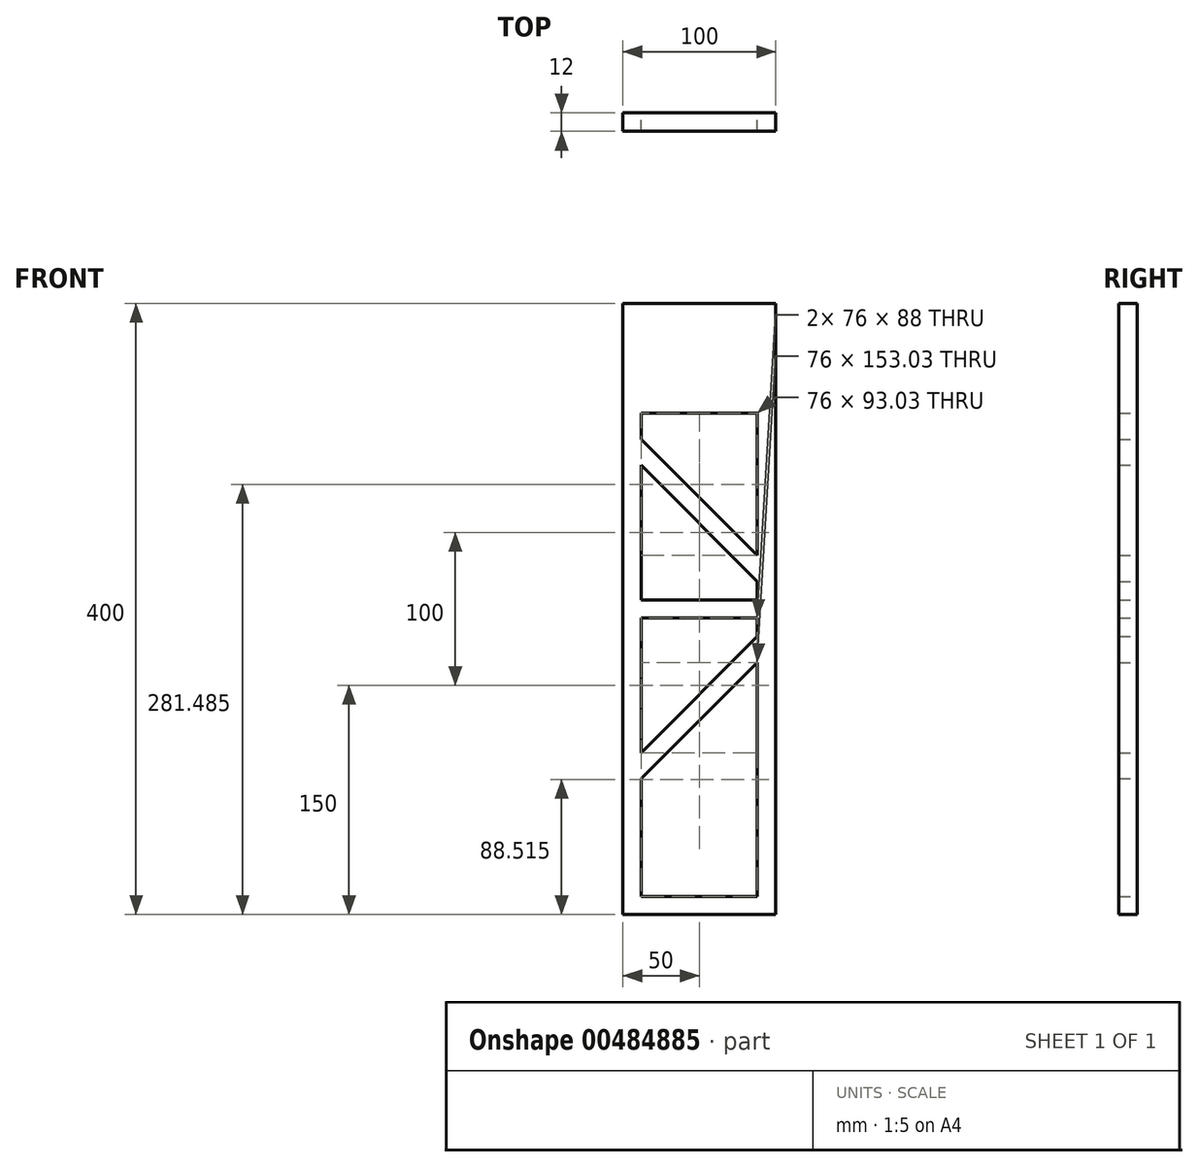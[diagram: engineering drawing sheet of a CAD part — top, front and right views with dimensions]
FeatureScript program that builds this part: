
annotation { "Feature Type Name" : "Feature", "Feature Type Description" : "" }
export const myFeature = defineFeature(function(context is Context, id is Id, definition is map)
    precondition{}
    {
        {
            var Q0;
            Q0=qCreatedBy(makeId("Front.planeOp"),FACE);
            var sketch = newSketch(context, id + "F0", { "sketchPlane" : qUnion([Q0])});
            skLineSegment(sketch, "E0", {"start": v(0, 0) * mm, "end": v(50, 0) * mm});
            skLineSegment(sketch, "E1", {"start": v(50, 0) * mm, "end": v(50, 400) * mm});
            skLineSegment(sketch, "E2", {"start": v(0, 0) * mm, "end": v(-50, 0) * mm});
            skLineSegment(sketch, "E3", {"start": v(-50, 0) * mm, "end": v(-50, 400) * mm});
            skLineSegment(sketch, "E4", {"start": v(-50, 400) * mm, "end": v(50, 400) * mm});
            skLineSegment(sketch, "E5", {"start": v(-50, 388) * mm, "end": v(-38, 388) * mm, "construction": true});
            skLineSegment(sketch, "E6", {"start": v(-38, 388) * mm, "end": v(-38, 400) * mm, "construction": true});
            skLineSegment(sketch, "E7", {"start": v(38, 400) * mm, "end": v(38, 388) * mm, "construction": true});
            skLineSegment(sketch, "E8", {"start": v(38, 388) * mm, "end": v(50, 388) * mm, "construction": true});
            skLineSegment(sketch, "E9", {"start": v(38, 0) * mm, "end": v(38, 12) * mm, "construction": true});
            skLineSegment(sketch, "E10", {"start": v(38, 12) * mm, "end": v(50, 12) * mm, "construction": true});
            skLineSegment(sketch, "E11", {"start": v(-50, 12) * mm, "end": v(-38, 12) * mm, "construction": true});
            skLineSegment(sketch, "E12", {"start": v(-38, 12) * mm, "end": v(-38, 0) * mm, "construction": true});
            skLineSegment(sketch, "E13", {"start": v(-38, 388) * mm, "end": v(38, 388) * mm});
            skLineSegment(sketch, "E14", {"start": v(38, 388) * mm, "end": v(38, 12) * mm});
            skLineSegment(sketch, "E15", {"start": v(-38, 12) * mm, "end": v(-38, 388) * mm});
            skLineSegment(sketch, "E16", {"start": v(-38, 12) * mm, "end": v(38, 12) * mm});
            skLineSegment(sketch, "E17", {"start": v(-38, 328) * mm, "end": v(38, 328) * mm});
            skLineSegment(sketch, "E18", {"start": v(-21.41, 388) * mm, "end": v(-21.41, 328) * mm, "construction": true});
            skLineSegment(sketch, "E19", {"start": v(-38, 200) * mm, "end": v(38, 200) * mm, "construction": true});
            skLineSegment(sketch, "E20", {"start": v(38, 182) * mm, "end": v(-38, 106) * mm});
            skLineSegment(sketch, "E21", {"start": v(38, 165.03) * mm, "end": v(-38, 89.03) * mm});
            skLineSegment(sketch, "E22", {"start": v(0, 144) * mm, "end": v(8.49, 135.51) * mm, "construction": true});
            skLineSegment(sketch, "E23", {"start": v(-38, 206) * mm, "end": v(38, 206) * mm});
            skLineSegment(sketch, "E24", {"start": v(-38, 194) * mm, "end": v(38, 194) * mm});
            skLineSegment(sketch, "E25", {"start": v(10.47, 200) * mm, "end": v(10.47, 206) * mm, "construction": true});
            skLineSegment(sketch, "E26", {"start": v(-14.52, 200) * mm, "end": v(-14.52, 194) * mm, "construction": true});
            skLineSegment(sketch, "E27", {"start": v(0, 144) * mm, "end": v(0, 194) * mm, "construction": true});
            skLineSegment(sketch, "E28", {"start": v(38, 218) * mm, "end": v(-38, 294) * mm});
            skLineSegment(sketch, "E29", {"start": v(0, 256) * mm, "end": v(0, 206) * mm, "construction": true});
            skLineSegment(sketch, "E30", {"start": v(-38, 310.97) * mm, "end": v(38, 234.97) * mm});
            skLineSegment(sketch, "E31", {"start": v(0, 256) * mm, "end": v(8.49, 264.49) * mm, "construction": true});
            skSolve(sketch);
        }
        {
            var Q0;
            Q0=makeQuery(id+"F0.imprint","IMPRINT",FACE,{"disambiguationData":[TD([[makeQuery(id+"F0.imprint","IMPRINT",EDGE,{"derivedFrom":sQuery(id+"F0.wireOp",EDGE,"E0")}),1.0]])]});
            var Q1;
            {var subQ0=sQuery(id+"F0.wireOp",EDGE,"E23");Q1=makeQuery(id+"F0.imprint","IMPRINT",FACE,{"disambiguationData":[TD([[makeQuery(id+"F0.imprint","IMPRINT",EDGE,{"derivedFrom":subQ0}),-1.0]])]});}
            var Q2;
            {var subQ0=sQuery(id+"F0.wireOp",EDGE,"E20");Q2=makeQuery(id+"F0.imprint","IMPRINT",FACE,{"disambiguationData":[TD([[makeQuery(id+"F0.imprint","IMPRINT",EDGE,{"derivedFrom":subQ0}),1.0]])]});}
            var Q3;
            {var subQ0=sQuery(id+"F0.wireOp",EDGE,"E28");Q3=makeQuery(id+"F0.imprint","IMPRINT",FACE,{"disambiguationData":[TD([[makeQuery(id+"F0.imprint","IMPRINT",EDGE,{"derivedFrom":subQ0}),-1.0]])]});}
            var Q4;
            {var subQ0=sQuery(id+"F0.wireOp",EDGE,"E13");Q4=makeQuery(id+"F0.imprint","IMPRINT",FACE,{"disambiguationData":[TD([[makeQuery(id+"F0.imprint","IMPRINT",EDGE,{"derivedFrom":subQ0}),-1.0]])]});}
            extrude(context, id + "F1", {"entities" : qUnion([Q0, Q1, Q2, Q3, Q4]), "depth" : 12 * mm, "offsetDistance" : 25 * mm});
        }
    });
